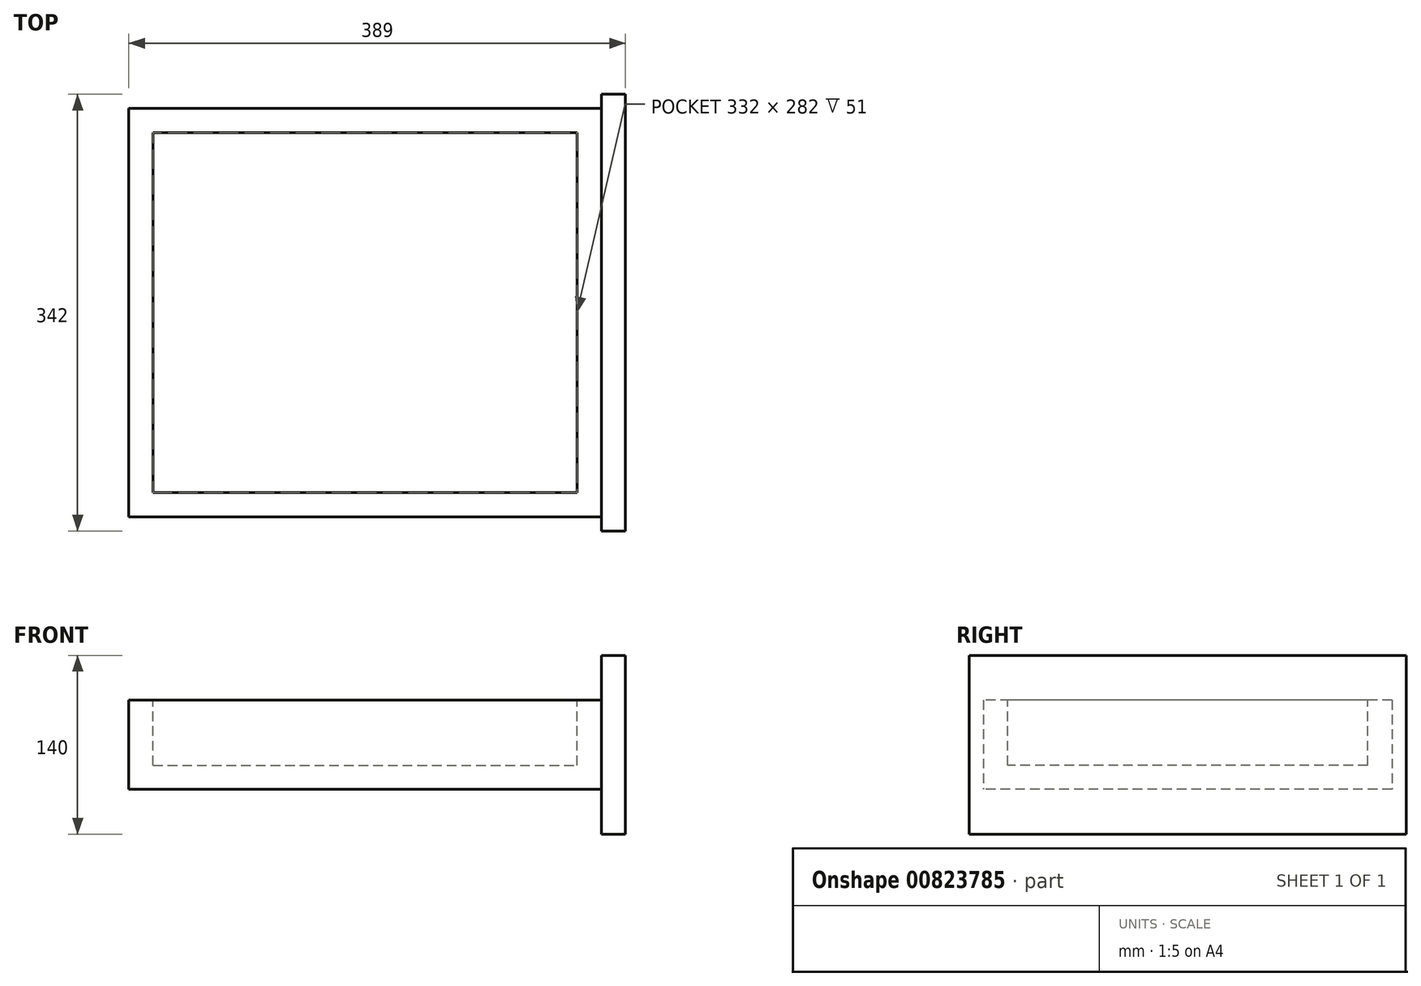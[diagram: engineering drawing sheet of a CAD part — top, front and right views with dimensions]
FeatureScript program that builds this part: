
annotation { "Feature Type Name" : "Feature", "Feature Type Description" : "" }
export const myFeature = defineFeature(function(context is Context, id is Id, definition is map)
    precondition{}
    {
        {
            var Q0;
            Q0=qCreatedBy(makeId("Top.planeOp"),FACE);
            var sketch = newSketch(context, id + "F0", { "sketchPlane" : qUnion([Q0])});
            skLineSegment(sketch, "E0.bottom", {"start": v(-185, 160) * mm, "end": v(185, 160) * mm});
            skLineSegment(sketch, "E0.top", {"start": v(-185, -160) * mm, "end": v(185, -160) * mm});
            skLineSegment(sketch, "E0.left", {"start": v(-185, 160) * mm, "end": v(-185, -160) * mm});
            skLineSegment(sketch, "E0.right", {"start": v(185, 160) * mm, "end": v(185, -160) * mm});
            skPoint(sketch, "E0.middle", {"position": v(0, 0) * mm});
            skSolve(sketch);
        }
        {
            var Q0;
            Q0=makeQuery(id+"F0.imprint","IMPRINT",FACE,{"disambiguationData":[TD([[makeQuery(id+"F0.imprint","IMPRINT",EDGE,{"derivedFrom":sQuery(id+"F0.wireOp",EDGE,"E0.bottom")}),-1.0]])]});
            extrude(context, id + "F1", {"entities" : qUnion([Q0]), "depth" : 70 * mm, "offsetDistance" : 25 * mm});
        }
        {
            var Q0;
            Q0=makeQuery(id+"F1.opExtrude","CAP_FACE",FACE,{"disambiguationData":[OSD([sQuery(id+"F0.wireOp",EDGE,"E0.bottom"),sQuery(id+"F0.wireOp",EDGE,"E0.top"),sQuery(id+"F0.wireOp",EDGE,"E0.left"),sQuery(id+"F0.wireOp",EDGE,"E0.right")])],"isStart":false});
            extrude(context, id + "F2", {"entities" : qUnion([Q0]), "operationType" : NewBodyOperationType.ADD, "depth" : -51 * mm, "offsetDistance" : 25 * mm});
        }
        {
            var Q0;
            Q0=makeQuery(id+"F1.opExtrude","CAP_FACE",FACE,{"disambiguationData":[OSD([sQuery(id+"F0.wireOp",EDGE,"E0.bottom"),sQuery(id+"F0.wireOp",EDGE,"E0.top"),sQuery(id+"F0.wireOp",EDGE,"E0.left"),sQuery(id+"F0.wireOp",EDGE,"E0.right")])],"isStart":false});
            var sketch = newSketch(context, id + "F3", { "sketchPlane" : qUnion([Q0])});
            skLineSegment(sketch, "E1.bottom", {"start": v(-166, 141) * mm, "end": v(166, 141) * mm});
            skLineSegment(sketch, "E1.top", {"start": v(-166, -141) * mm, "end": v(166, -141) * mm});
            skLineSegment(sketch, "E1.left", {"start": v(-166, 141) * mm, "end": v(-166, -141) * mm});
            skLineSegment(sketch, "E1.right", {"start": v(166, 141) * mm, "end": v(166, -141) * mm});
            skPoint(sketch, "E1.middle", {"position": v(0, 0) * mm});
            skSolve(sketch);
        }
        {
            var Q0;
            Q0=makeQuery(id+"F3.imprint","IMPRINT",FACE,{"disambiguationData":[TD([[makeQuery(id+"F3.imprint","IMPRINT",EDGE,{"derivedFrom":sQuery(id+"F3.wireOp",EDGE,"E1.bottom")}),-1.0]])]});
            extrude(context, id + "F4", {"entities" : qUnion([Q0]), "operationType" : NewBodyOperationType.REMOVE, "oppositeDirection" : true, "depth" : 51 * mm, "offsetDistance" : 25 * mm});
        }
        {
            var Q0;
            Q0=makeQuery(id+"F1.opExtrude","SWEPT_FACE",FACE,{"disambiguationData":[OSD([sQuery(id+"F0.wireOp",EDGE,"E0.right")])]});
            var sketch = newSketch(context, id + "F5", { "sketchPlane" : qUnion([Q0])});
            skLineSegment(sketch, "E2.bottom", {"start": v(171, 105) * mm, "end": v(-171, 105) * mm});
            skLineSegment(sketch, "E2.top", {"start": v(171, -35) * mm, "end": v(-171, -35) * mm});
            skLineSegment(sketch, "E2.left", {"start": v(171, 105) * mm, "end": v(171, -35) * mm});
            skLineSegment(sketch, "E2.right", {"start": v(-171, 105) * mm, "end": v(-171, -35) * mm});
            skPoint(sketch, "E2.middle", {"position": v(0, 35) * mm});
            skPoint(sketch, "E2.middle.positionSnap0", {"position": v(0, 0) * mm});
            skPoint(sketch, "E2.middle.positionSnap1", {"position": v(-160, 35) * mm});
            skPoint(sketch, "E2.centerSnap0", {"position": v(0, 0) * mm});
            skPoint(sketch, "E2.centerSnap1", {"position": v(-160, 35) * mm});
            skSolve(sketch);
        }
        {
            var Q0;
            Q0 = qSketchRegion(id + "F5", true);
            extrude(context, id + "F6", {"entities" : qUnion([Q0]), "operationType" : NewBodyOperationType.ADD, "depth" : 19 * mm, "offsetDistance" : 25 * mm});
        }
    });
